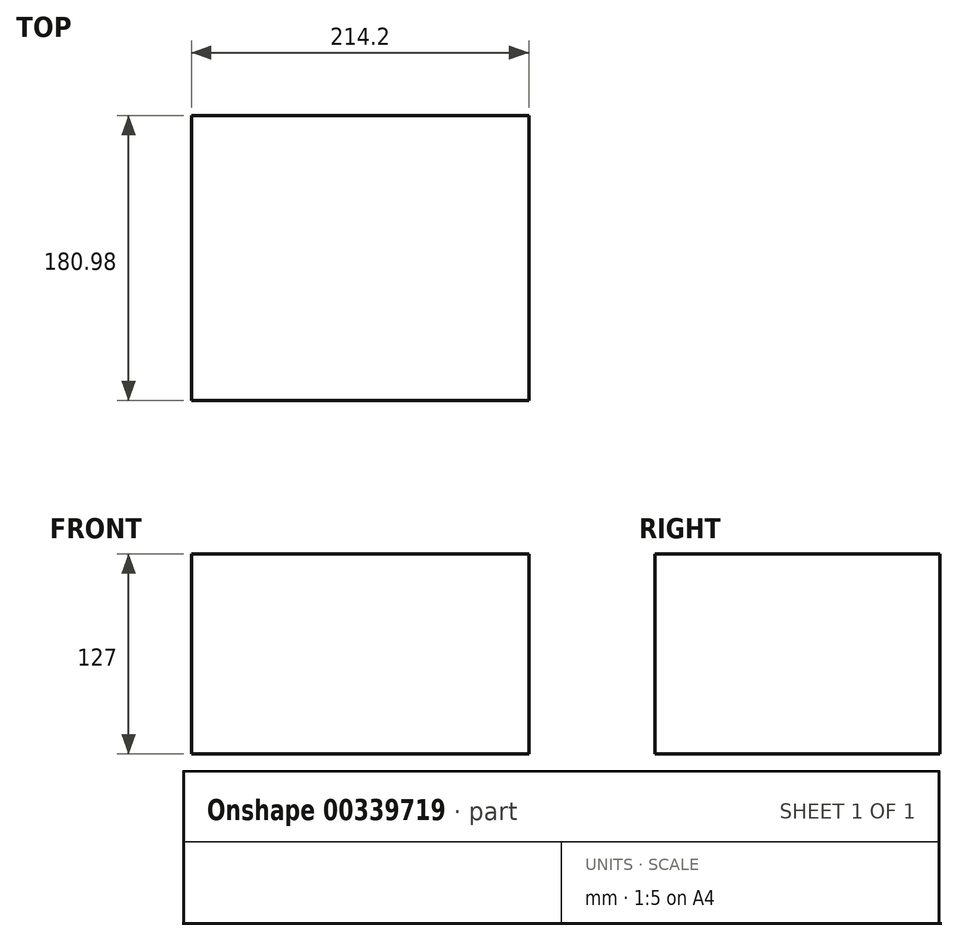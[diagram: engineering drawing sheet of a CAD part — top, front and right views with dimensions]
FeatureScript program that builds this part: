
annotation { "Feature Type Name" : "Feature", "Feature Type Description" : "" }
export const myFeature = defineFeature(function(context is Context, id is Id, definition is map)
    precondition{}
    {
        {
            var Q0;
            Q0=qCreatedBy(makeId("Top.planeOp"),FACE);
            var sketch = newSketch(context, id + "F0", { "sketchPlane" : qUnion([Q0])});
            skLineSegment(sketch, "E0.bottom", {"start": v(107.1, 90.49) * mm, "end": v(-107.1, 90.49) * mm});
            skLineSegment(sketch, "E0.top", {"start": v(107.1, -90.49) * mm, "end": v(-107.1, -90.49) * mm});
            skLineSegment(sketch, "E0.left", {"start": v(107.1, 90.49) * mm, "end": v(107.1, -90.49) * mm});
            skLineSegment(sketch, "E0.right", {"start": v(-107.1, 90.49) * mm, "end": v(-107.1, -90.49) * mm});
            skPoint(sketch, "E0.middle", {"position": v(0, 0) * mm});
            skSolve(sketch);
        }
        {
            var Q0;
            Q0=makeQuery(id+"F0.imprint","IMPRINT",FACE,{"disambiguationData":[TD([[makeQuery(id+"F0.imprint","IMPRINT",EDGE,{"derivedFrom":sQuery(id+"F0.wireOp",EDGE,"E0.bottom")}),1.0]])]});
            extrude(context, id + "F1", {"entities" : qUnion([Q0]), "depth" : 127 * mm});
        }
    });
